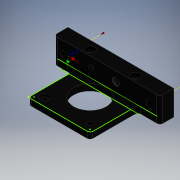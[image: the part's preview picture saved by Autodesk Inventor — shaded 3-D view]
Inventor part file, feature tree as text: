
AUTODESK INVENTOR PART (.ipt)
format: ipt  version: 2016 SP1 (Build 200210100, 210)  size: 167,936 bytes
history: native  units: mm
features: sketch x11, other x3, plane x1
ambient origin geometry x8: Origin, YZ Plane, XZ Plane, XY Plane, X Axis, Y Axis, Z Axis, Center Point
bodies: Solid1 (feature_tree)
feature tree (15):
  other  "Part1.ipt"
  other  "Solid1::Part1.ipt"
  other  "TaggingFeature1"
  sketch  "Sketch1"  dims[d0=10.0mm]
  sketch  "Sketch2"
  sketch  "Sketch3"
  sketch  "Sketch4"
  sketch  "Sketch5"
  sketch  "Sketch6"
  sketch  "Sketch7"
  sketch  "Sketch8"
  sketch  "Sketch9"
  sketch  "Sketch10"
  sketch  "Sketch11"
  plane  "Work Plane1"
